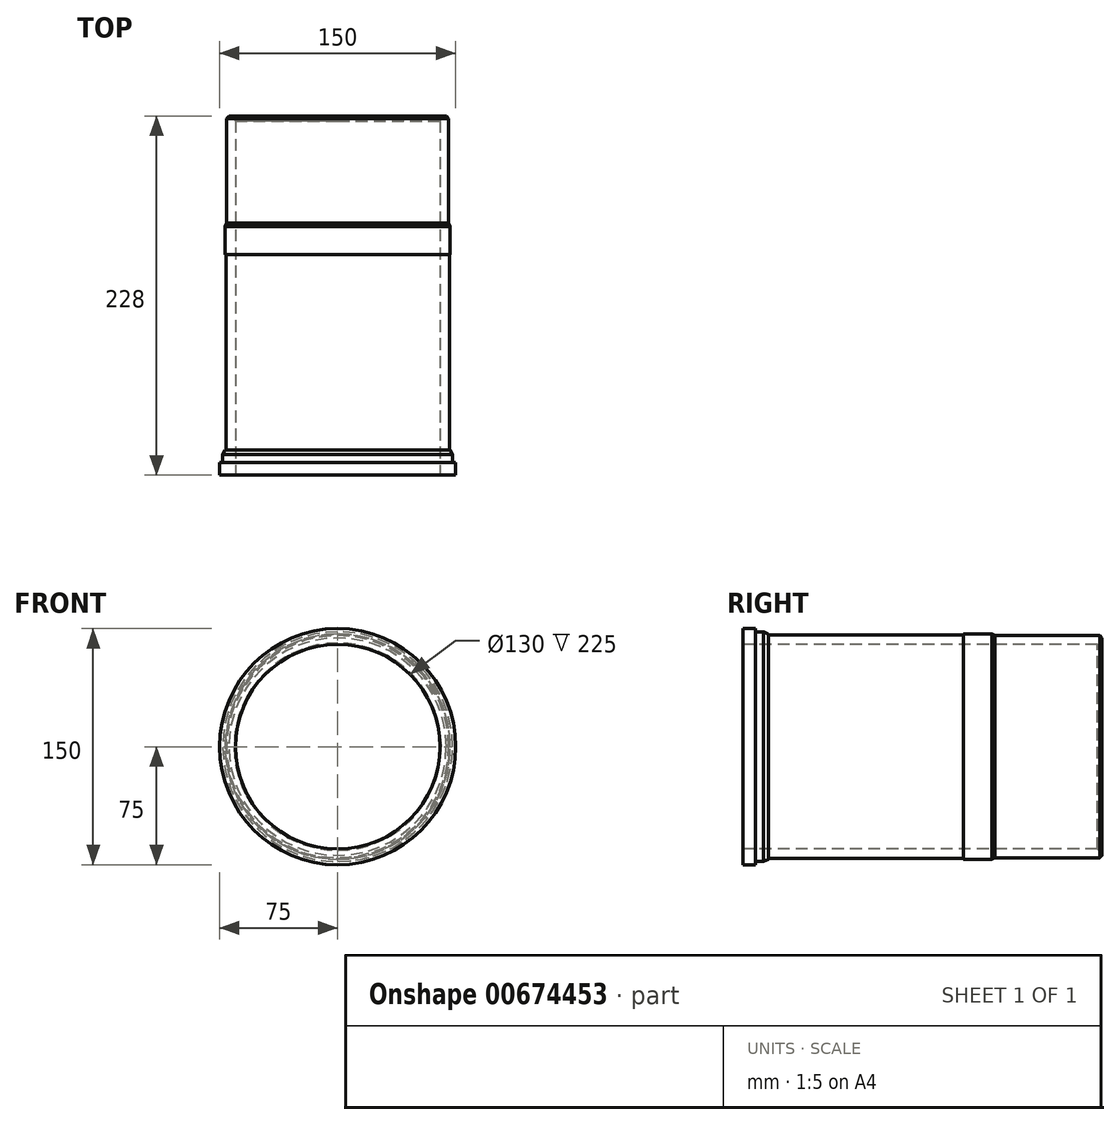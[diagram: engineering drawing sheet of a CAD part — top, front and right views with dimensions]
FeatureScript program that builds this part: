
annotation { "Feature Type Name" : "Feature", "Feature Type Description" : "" }
export const myFeature = defineFeature(function(context is Context, id is Id, definition is map)
    precondition{}
    {
        {
            var Q0;
            Q0=qCreatedBy(makeId("Right.planeOp"),FACE);
            var sketch = newSketch(context, id + "F0", { "sketchPlane" : qUnion([Q0])});
            skLineSegment(sketch, "E0", {"start": v(0, 0) * mm, "end": v(0, 75) * mm});
            skLineSegment(sketch, "E1", {"start": v(0, 75) * mm, "end": v(8, 75) * mm});
            skLineSegment(sketch, "E2", {"start": v(8, 75) * mm, "end": v(8, 73) * mm});
            skLineSegment(sketch, "E3", {"start": v(8, 73) * mm, "end": v(16, 73) * mm});
            skLineSegment(sketch, "E4", {"start": v(0, 65) * mm, "end": v(228, 65) * mm});
            skLineSegment(sketch, "E5", {"start": v(228, 65) * mm, "end": v(228, 70.5) * mm});
            skLineSegment(sketch, "E6", {"start": v(228, 70.5) * mm, "end": v(149.6, 70.5) * mm});
            skLineSegment(sketch, "E7", {"start": v(0, 0) * mm, "end": v(88.78, 0) * mm});
            skLineSegment(sketch, "E8", {"start": v(16, 73) * mm, "end": v(16, 71) * mm});
            skLineSegment(sketch, "E9", {"start": v(16, 71) * mm, "end": v(140, 71) * mm});
            skLineSegment(sketch, "E10", {"start": v(140, 71) * mm, "end": v(140, 71.5) * mm});
            skLineSegment(sketch, "E11", {"start": v(140, 71.5) * mm, "end": v(160, 71.5) * mm});
            skLineSegment(sketch, "E12", {"start": v(160, 71.5) * mm, "end": v(160, 69.58) * mm});
            skSolve(sketch);
        }
        {
            var Q0;
            {var subQ0=sQuery(id+"F0.wireOp",EDGE,"E1");Q0=makeQuery(id+"F0.imprint","IMPRINT",FACE,{"disambiguationData":[TD([[makeQuery(id+"F0.imprint","IMPRINT",EDGE,{"derivedFrom":subQ0}),-1.0]])]});}
            var Q1;
            Q1=sQuery(id+"F0.wireOp",EDGE,"E7");
            revolve(context, id + "F1", {"entities" : qUnion([Q0]), "axis" : qUnion([Q1]), "revolveType" : RevolveType.FULL});
        }
        {
            var Q0;
            Q0=makeQuery(id+"F1.opRevolve","SWEPT_EDGE",EDGE,{"disambiguationData":[OSD([sQuery(id+"F0.wireOp",EDGE,"E4"),sQuery(id+"F0.wireOp",EDGE,"E5")])]});
            chamfer(context, id + "F2", {"entities" : qUnion([Q0]), "chamferType" : ChamferType.OFFSET_ANGLE, "width" : 3 * mm, "oppositeDirection" : true, "angle" : 15 * degree, "tangentPropagation" : true});
        }
        {
            var Q0;
            Q0=makeQuery(id+"F1.opRevolve","SWEPT_EDGE",EDGE,{"disambiguationData":[OSD([sQuery(id+"F0.wireOp",EDGE,"E5"),sQuery(id+"F0.wireOp",EDGE,"E6")])]});
            chamfer(context, id + "F3", {"entities" : qUnion([Q0]), "width" : 1.5 * mm, "tangentPropagation" : true});
        }
        {
            var Q0;
            Q0=makeQuery(id+"F1.opRevolve","SWEPT_EDGE",EDGE,{"disambiguationData":[OSD([sQuery(id+"F0.wireOp",EDGE,"E11"),sQuery(id+"F0.wireOp",EDGE,"E12")])]});
            chamfer(context, id + "F4", {"entities" : qUnion([Q0]), "chamferType" : ChamferType.TWO_OFFSETS, "width1" : 2 * mm, "oppositeDirection" : false, "width2" : 1 * mm, "tangentPropagation" : true});
        }
        {
            var Q0;
            Q0=makeQuery(id+"F1.opRevolve","SWEPT_EDGE",EDGE,{"disambiguationData":[OSD([sQuery(id+"F0.wireOp",EDGE,"E3"),sQuery(id+"F0.wireOp",EDGE,"E8")])]});
            chamfer(context, id + "F5", {"entities" : qUnion([Q0]), "chamferType" : ChamferType.TWO_OFFSETS, "width1" : 3 * mm, "oppositeDirection" : false, "width2" : 1.5 * mm, "tangentPropagation" : true});
        }
    });
